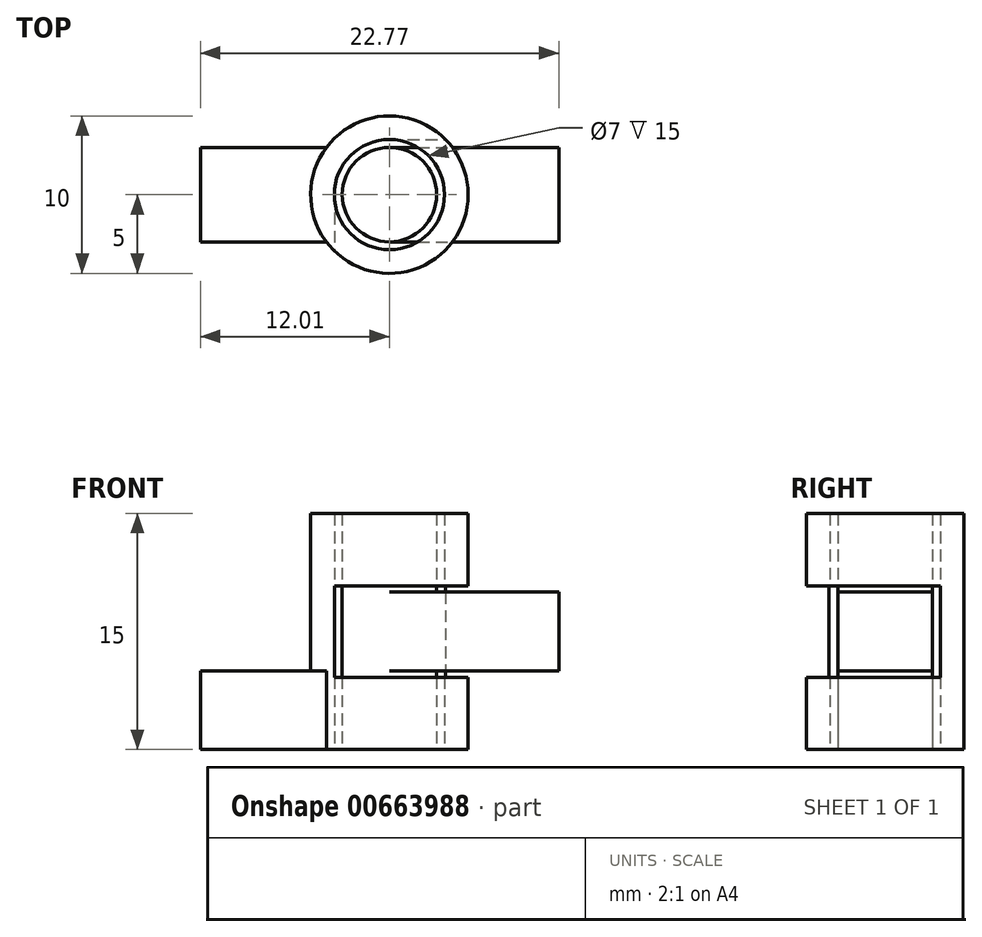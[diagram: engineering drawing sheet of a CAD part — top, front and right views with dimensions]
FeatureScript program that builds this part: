
annotation { "Feature Type Name" : "Feature", "Feature Type Description" : "" }
export const myFeature = defineFeature(function(context is Context, id is Id, definition is map)
    precondition{}
    {
        {
            var Q0;
            Q0=qCreatedBy(makeId("Top.planeOp"),FACE);
            var sketch = newSketch(context, id + "F0", { "sketchPlane" : qUnion([Q0])});
            skCircle(sketch, "E0", {"center": v(0, 0) * mm, "radius": 3 * mm});
            skLineSegment(sketch, "E1", {"start": v(0, 3) * mm, "end": v(10.76, 3) * mm});
            skLineSegment(sketch, "E2", {"start": v(0, -3) * mm, "end": v(10.76, -3) * mm});
            skLineSegment(sketch, "E3", {"start": v(10.76, -3) * mm, "end": v(10.76, 3) * mm});
            skCircle(sketch, "E4", {"center": v(0, 0) * mm, "radius": 3.5 * mm});
            skCircle(sketch, "E5", {"center": v(0, 0) * mm, "radius": 5 * mm});
            skLineSegment(sketch, "E6", {"start": v(-4, 3) * mm, "end": v(-12, 3) * mm});
            skLineSegment(sketch, "E7", {"start": v(-4, -3) * mm, "end": v(-12, -3) * mm});
            skLineSegment(sketch, "E8", {"start": v(-12, -3) * mm, "end": v(-12, 3) * mm});
            skSolve(sketch);
        }
        {
            var Q0;
            {var subQ0=sQuery(id+"F0.wireOp",EDGE,"E0");var subQ1=makeQuery(id+"F0.imprint","INTERSECT",VERTEX,{"derivedFrom":[subQ0,sQuery(id+"F0.wireOp",EDGE,"E1")]});Q0=makeQuery(id+"F0.imprint","IMPRINT",FACE,{"disambiguationData":[TD([[makeQuery(id+"F0.imprint","IMPRINT",EDGE,{"disambiguationData":[TD([[subQ1,-1.0]])],"derivedFrom":subQ0}),1.0]])]});}
            extrude(context, id + "F1", {"entities" : qUnion([Q0]), "depth" : 15 * mm, "offsetDistance" : 25 * mm});
        }
        {
            var Q0;
            {var subQ0=sQuery(id+"F0.wireOp",EDGE,"E3");Q0=makeQuery(id+"F0.imprint","IMPRINT",FACE,{"disambiguationData":[TD([[makeQuery(id+"F0.imprint","IMPRINT",EDGE,{"derivedFrom":subQ0}),1.0]])]});}
            var Q1;
            {var subQ0=sQuery(id+"F0.wireOp",EDGE,"E1");var subQ1=sQuery(id+"F0.wireOp",EDGE,"E0");var subQ2=makeQuery(id+"F0.imprint","INTERSECT",VERTEX,{"derivedFrom":[subQ1,subQ0]});Q1=makeQuery(id+"F0.imprint","IMPRINT",FACE,{"disambiguationData":[TD([[makeQuery(id+"F0.imprint","IMPRINT",EDGE,{"disambiguationData":[TD([[subQ2,1.0]])],"derivedFrom":subQ1}),-1.0]])]});}
            var Q2;
            {var subQ0=sQuery(id+"F0.wireOp",EDGE,"E5");var subQ1=sQuery(id+"F0.wireOp",EDGE,"E1");var subQ2=makeQuery(id+"F0.imprint","INTERSECT",VERTEX,{"derivedFrom":[subQ1,subQ0]});Q2=makeQuery(id+"F0.imprint","IMPRINT",FACE,{"disambiguationData":[TD([[makeQuery(id+"F0.imprint","IMPRINT",EDGE,{"disambiguationData":[TD([[subQ2,1.0]])],"derivedFrom":subQ1}),-1.0]])]});}
            extrude(context, id + "F2", {"entities" : qUnion([Q0, Q1, Q2]), "operationType" : NewBodyOperationType.ADD, "depth" : 10 * mm, "offsetDistance" : 25 * mm, "hasSecondDirection" : true, "secondDirectionOppositeDirection" : false, "secondDirectionDepth" : 5 * mm});
        }
        {
            var Q0;
            {var subQ1=sQuery(id+"F0.wireOp",EDGE,"E1");var subQ5=sQuery(id+"F0.wireOp",EDGE,"E5");var subQ7=makeQuery(id+"F0.imprint","INTERSECT",VERTEX,{"derivedFrom":[subQ1,subQ5]});Q0=makeQuery(id+"F0.imprint","IMPRINT",FACE,{"disambiguationData":[TD([[makeQuery(id+"F0.imprint","IMPRINT",EDGE,{"disambiguationData":[TD([[subQ7,1.0]])],"derivedFrom":subQ1}),1.0]])]});}
            var Q1;
            {var subQ0=sQuery(id+"F0.wireOp",EDGE,"E5");var subQ1=sQuery(id+"F0.wireOp",EDGE,"E1");var subQ2=makeQuery(id+"F0.imprint","INTERSECT",VERTEX,{"derivedFrom":[subQ1,subQ0]});Q1=makeQuery(id+"F0.imprint","IMPRINT",FACE,{"disambiguationData":[TD([[makeQuery(id+"F0.imprint","IMPRINT",EDGE,{"disambiguationData":[TD([[subQ2,1.0]])],"derivedFrom":subQ1}),-1.0]])]});}
            extrude(context, id + "F3", {"entities" : qUnion([Q0, Q1]), "depth" : 4.6 * mm, "offsetDistance" : 25 * mm});
        }
        {
            var Q0;
            Q0=makeQuery(id+"F3.opExtrude","CAP_FACE",FACE,{"disambiguationData":[OSD([sQuery(id+"F0.wireOp",EDGE,"E4"),sQuery(id+"F0.wireOp",EDGE,"E5")])],"isStart":false});
            var sketch = newSketch(context, id + "F4", { "sketchPlane" : qUnion([Q0])});
            skLineSegment(sketch, "E9", {"start": v(0, 5) * mm, "end": v(0, 3.5) * mm});
            skLineSegment(sketch, "E10", {"start": v(0, 3.5) * mm, "end": v(3.57, 3.5) * mm});
            skLineSegment(sketch, "E11", {"start": v(-5, 0) * mm, "end": v(-3.5, 0) * mm});
            skLineSegment(sketch, "E12", {"start": v(-3.5, 0) * mm, "end": v(-3.5, -3.57) * mm});
            skCircle(sketch, "E13", {"center": v(0, 0) * mm, "radius": 5 * mm});
            skSolve(sketch);
        }
        {
            var Q0;
            {var subQ0=sQuery(id+"F4.wireOp",EDGE,"E11");Q0=makeQuery(id+"F4.imprint","IMPRINT",FACE,{"disambiguationData":[TD([[makeQuery(id+"F4.imprint","IMPRINT",EDGE,{"derivedFrom":subQ0}),-1.0]])]});}
            var Q1;
            {var subQ0=sQuery(id+"F4.wireOp",EDGE,"E9");Q1=makeQuery(id+"F4.imprint","IMPRINT",FACE,{"disambiguationData":[TD([[makeQuery(id+"F4.imprint","IMPRINT",EDGE,{"derivedFrom":subQ0}),-1.0]])]});}
            var Q2;
            {var subQ0=sQuery(id+"F4.wireOp",EDGE,"E9");Q2=makeQuery(id+"F4.imprint","IMPRINT",FACE,{"disambiguationData":[TD([[makeQuery(id+"F4.imprint","IMPRINT",EDGE,{"derivedFrom":subQ0}),1.0]])]});}
            extrude(context, id + "F5", {"entities" : qUnion([Q0, Q1, Q2]), "operationType" : NewBodyOperationType.ADD, "depth" : 5.8 * mm, "offsetDistance" : 25 * mm});
        }
        {
            var Q0;
            {var subQ1=sQuery(id+"F0.wireOp",EDGE,"E1");var subQ5=sQuery(id+"F0.wireOp",EDGE,"E5");var subQ7=makeQuery(id+"F0.imprint","INTERSECT",VERTEX,{"derivedFrom":[subQ1,subQ5]});Q0=makeQuery(id+"F0.imprint","IMPRINT",FACE,{"disambiguationData":[TD([[makeQuery(id+"F0.imprint","IMPRINT",EDGE,{"disambiguationData":[TD([[subQ7,1.0]])],"derivedFrom":subQ1}),1.0]])]});}
            var Q1;
            {var subQ0=sQuery(id+"F0.wireOp",EDGE,"E5");var subQ1=sQuery(id+"F0.wireOp",EDGE,"E1");var subQ2=makeQuery(id+"F0.imprint","INTERSECT",VERTEX,{"derivedFrom":[subQ1,subQ0]});Q1=makeQuery(id+"F0.imprint","IMPRINT",FACE,{"disambiguationData":[TD([[makeQuery(id+"F0.imprint","IMPRINT",EDGE,{"disambiguationData":[TD([[subQ2,1.0]])],"derivedFrom":subQ1}),-1.0]])]});}
            var Q2;
            Q2=makeQuery(id+"F1.opExtrude","CAP_FACE",FACE,{"disambiguationData":[OSD([sQuery(id+"F0.wireOp",EDGE,"E0")])],"isStart":false});
            var Q3;
            Q3=makeQuery(id+"F5.opExtrude","CAP_FACE",FACE,{"disambiguationData":[OSD([sQuery(id+"F0.wireOp",EDGE,"E4"),sQuery(id+"F4.wireOp",EDGE,"E10"),sQuery(id+"F4.wireOp",EDGE,"E12"),sQuery(id+"F4.wireOp",EDGE,"E13")])],"isStart":false});
            extrude(context, id + "F6", {"entities" : qUnion([Q0, Q1]), "operationType" : NewBodyOperationType.ADD, "endBound" : BoundingType.UP_TO_SURFACE, "depth" : 16.1 * mm, "endBoundEntityFace" : qUnion([Q2]), "offsetDistance" : 25 * mm, "hasSecondDirection" : true, "secondDirectionBound" : SecondDirectionBoundingType.UP_TO_SURFACE, "secondDirectionOppositeDirection" : false, "secondDirectionDepth" : 10.3 * mm, "secondDirectionBoundEntityFace" : qUnion([Q3])});
        }
        {
            var Q0;
            {var subQ0=sQuery(id+"F0.wireOp",EDGE,"E6");Q0=makeQuery(id+"F0.imprint","IMPRINT",FACE,{"disambiguationData":[TD([[makeQuery(id+"F0.imprint","IMPRINT",EDGE,{"derivedFrom":subQ0}),1.0]])]});}
            extrude(context, id + "F7", {"entities" : qUnion([Q0]), "operationType" : NewBodyOperationType.ADD, "depth" : 5 * mm, "offsetDistance" : 25 * mm});
        }
    });
